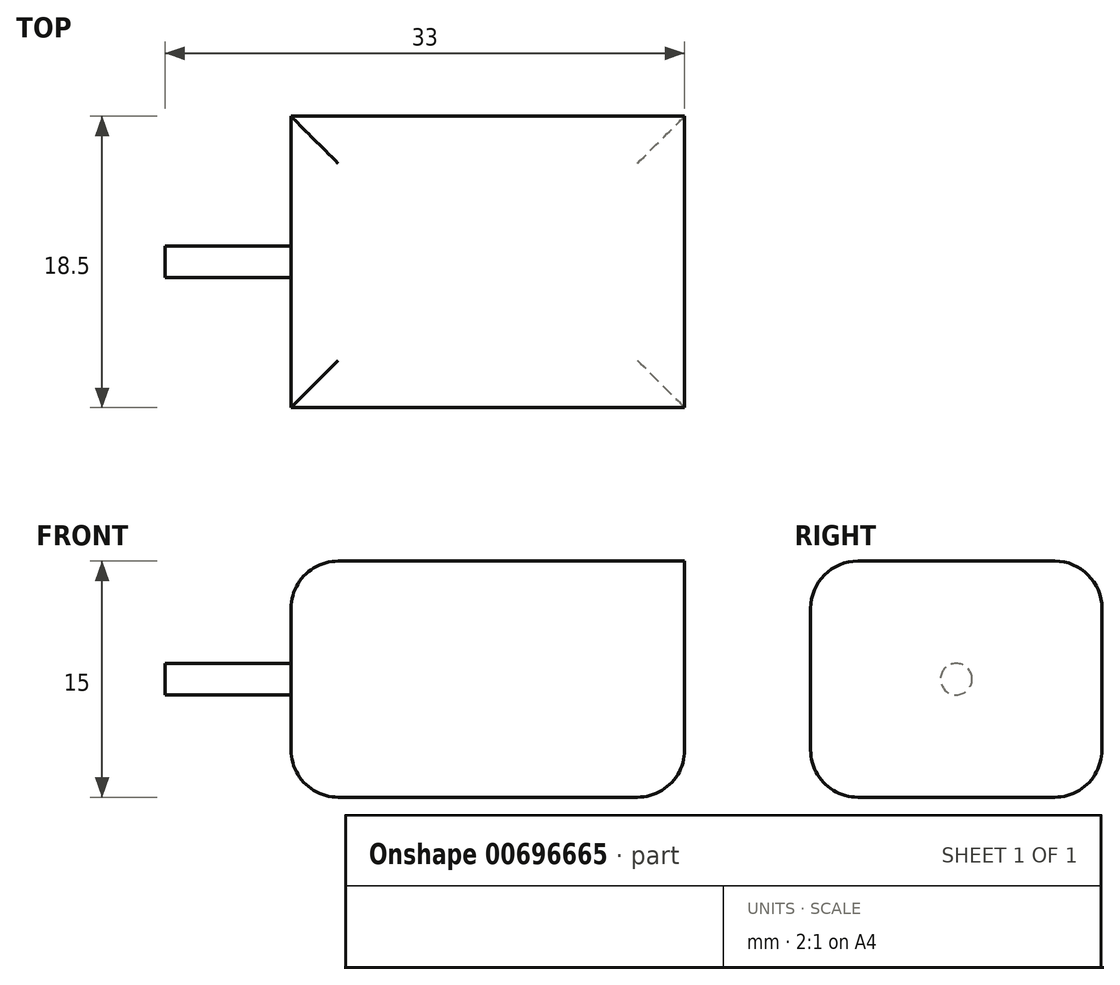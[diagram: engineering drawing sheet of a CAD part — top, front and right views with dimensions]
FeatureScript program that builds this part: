
annotation { "Feature Type Name" : "Feature", "Feature Type Description" : "" }
export const myFeature = defineFeature(function(context is Context, id is Id, definition is map)
    precondition{}
    {
        {
            var Q0;
            Q0=qCreatedBy(makeId("Front.planeOp"),FACE);
            var sketch = newSketch(context, id + "F0", { "sketchPlane" : qUnion([Q0])});
            skLineSegment(sketch, "E0.bottom", {"start": v(-21.68, 0) * mm, "end": v(3.32, 0) * mm});
            skLineSegment(sketch, "E0.top", {"start": v(-21.68, 15) * mm, "end": v(3.32, 15) * mm});
            skLineSegment(sketch, "E0.left", {"start": v(-21.68, 0) * mm, "end": v(-21.68, 15) * mm});
            skLineSegment(sketch, "E0.right", {"start": v(3.32, 0) * mm, "end": v(3.32, 15) * mm});
            skSolve(sketch);
        }
        {
            var Q0;
            Q0=makeQuery(id+"F0.imprint","IMPRINT",FACE,{"disambiguationData":[TD([[makeQuery(id+"F0.imprint","IMPRINT",EDGE,{"derivedFrom":sQuery(id+"F0.wireOp",EDGE,"E0.bottom")}),1.0]])]});
            extrude(context, id + "F1", {"entities" : qUnion([Q0]), "depth" : 18.5 * mm, "offsetDistance" : 25 * mm});
        }
        {
            var Q0;
            Q0=makeQuery(id+"F1.opExtrude","CAP_EDGE",EDGE,{"disambiguationData":[OSD([sQuery(id+"F0.wireOp",EDGE,"E0.top")])],"isStart":false});
            var Q1;
            Q1=makeQuery(id+"F1.opExtrude","CAP_EDGE",EDGE,{"disambiguationData":[OSD([sQuery(id+"F0.wireOp",EDGE,"E0.top")])],"isStart":true});
            var Q2;
            Q2=makeQuery(id+"F1.opExtrude","CAP_EDGE",EDGE,{"disambiguationData":[OSD([sQuery(id+"F0.wireOp",EDGE,"E0.bottom")])],"isStart":false});
            var Q3;
            Q3=makeQuery(id+"F1.opExtrude","CAP_EDGE",EDGE,{"disambiguationData":[OSD([sQuery(id+"F0.wireOp",EDGE,"E0.bottom")])],"isStart":true});
            var Q4;
            Q4=makeQuery(id+"F1.opExtrude","SWEPT_EDGE",EDGE,{"disambiguationData":[OSD([sQuery(id+"F0.wireOp",EDGE,"E0.bottom"),sQuery(id+"F0.wireOp",EDGE,"E0.left")])]});
            var Q5;
            Q5=makeQuery(id+"F1.opExtrude","SWEPT_EDGE",EDGE,{"disambiguationData":[OSD([sQuery(id+"F0.wireOp",EDGE,"E0.bottom"),sQuery(id+"F0.wireOp",EDGE,"E0.right")])]});
            var Q6;
            Q6=makeQuery(id+"F1.opExtrude","SWEPT_EDGE",EDGE,{"disambiguationData":[OSD([sQuery(id+"F0.wireOp",EDGE,"E0.top"),sQuery(id+"F0.wireOp",EDGE,"E0.left")])]});
            fillet(context, id + "F2", {"entities" : qUnion([Q0, Q1, Q2, Q3, Q4, Q5, Q6]), "radius" : 3 * mm, "tangentPropagation" : true, "defaultsChanged" : false, "allowEdgeOverflow" : false, "vertexSettings" : []});
        }
        {
            var Q0;
            Q0=makeQuery(id+"F1.opExtrude","SWEPT_FACE",FACE,{"disambiguationData":[OSD([sQuery(id+"F0.wireOp",EDGE,"E0.left")])]});
            var sketch = newSketch(context, id + "F3", { "sketchPlane" : qUnion([Q0])});
            skCircle(sketch, "E1", {"center": v(9.25, 7.5) * mm, "radius": 1 * mm});
            skPoint(sketch, "E2", {"position": v(18.5, 7.5) * mm});
            skLineSegment(sketch, "E3", {"start": v(9.25, 12) * mm, "end": v(9.25, 3) * mm, "construction": true});
            skSolve(sketch);
        }
        {
            var Q0;
            Q0=makeQuery(id+"F3.imprint","IMPRINT",FACE,{"disambiguationData":[TD([[makeQuery(id+"F3.imprint","IMPRINT",EDGE,{"derivedFrom":sQuery(id+"F3.wireOp",EDGE,"E1")}),1.0]])]});
            extrude(context, id + "F4", {"entities" : qUnion([Q0]), "operationType" : NewBodyOperationType.ADD, "flatOperationType" : FlatOperationType.REMOVE, "depth" : 8 * mm, "offsetDistance" : 25 * mm, "domain" : OperationDomain.MODEL});
        }
    });
